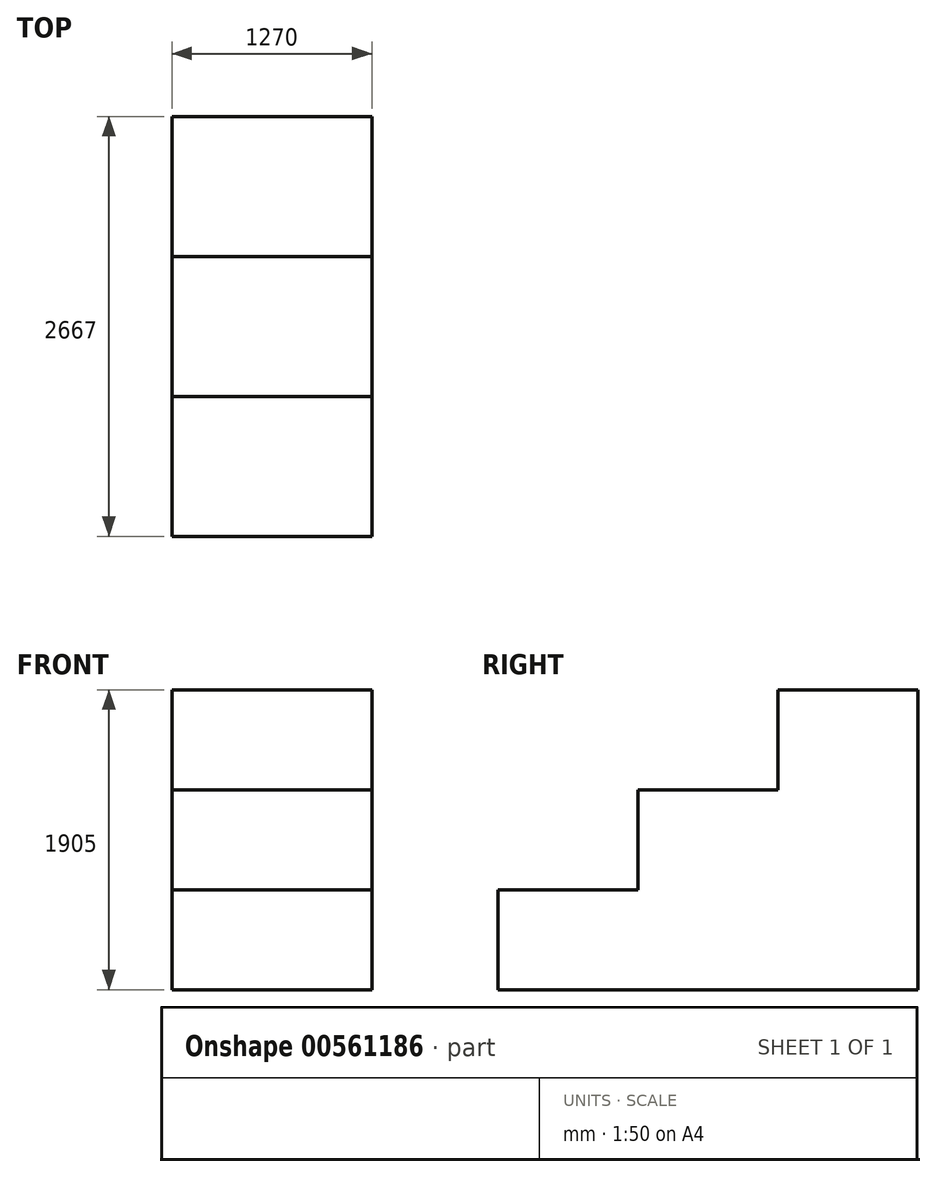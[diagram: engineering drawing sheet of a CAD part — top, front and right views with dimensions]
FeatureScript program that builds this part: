
annotation { "Feature Type Name" : "Feature", "Feature Type Description" : "" }
export const myFeature = defineFeature(function(context is Context, id is Id, definition is map)
    precondition{}
    {
        {
            var Q0;
            Q0=qCreatedBy(makeId("Right.planeOp"),FACE);
            var sketch = newSketch(context, id + "F0", { "sketchPlane" : qUnion([Q0])});
            skLineSegment(sketch, "E0", {"start": v(-1354.29, -1178.98) * mm, "end": v(1312.71, -1178.98) * mm});
            skLineSegment(sketch, "E1", {"start": v(1312.71, -1178.98) * mm, "end": v(1312.71, 726.02) * mm});
            skLineSegment(sketch, "E2", {"start": v(1312.71, 726.02) * mm, "end": v(423.71, 726.02) * mm});
            skLineSegment(sketch, "E3", {"start": v(423.71, 726.02) * mm, "end": v(423.71, 91.02) * mm});
            skLineSegment(sketch, "E4", {"start": v(423.71, 91.02) * mm, "end": v(-465.29, 91.02) * mm});
            skLineSegment(sketch, "E5", {"start": v(-465.29, 91.02) * mm, "end": v(-465.29, -543.98) * mm});
            skLineSegment(sketch, "E6", {"start": v(-465.29, -543.98) * mm, "end": v(-1354.29, -543.98) * mm});
            skLineSegment(sketch, "E7", {"start": v(-1354.29, -543.98) * mm, "end": v(-1354.29, -1178.98) * mm});
            skSolve(sketch);
        }
        {
            var Q0;
            Q0 = qSketchRegion(id + "F0", true);
            extrude(context, id + "F1", {"entities" : qUnion([Q0]), "depth" : 1270 * mm, "offsetDistance" : 25.4 * mm});
        }
    });
